# Revit family: Bathtub-American_Standard-Town_Square_Suite-2748_Series
name_source: partatom
category: Plumbing Fixtures
revit_build: Autodesk Revit 2014 (Build: 20130308_1515(x64)
units: mm (PartAtom-declared; Revit-internal decimal feet)

## types (9) — shared parameters
Apron: 9460.018 (specify color) = No
Assembly Code = D2010510
CW Connection = Yes
CWFU = 3
Default Elevation = 0"
Description = TOWN SQUARE® 5' x 42" WHIRLPOOL AND BATHING POOL HIGH GLOSS
EverClean = No
HW Connection = Yes
HWFU = 3
Height = 23"
Length = 41 5/8"
Manufacturer = American Standard
Model = 2748.002.011
Outlet Diameter = 1 1/2"
Outlet Location = 14 1/2"
Product Documentation Link = https://www.americanstandard-us.com
Product Page URL = https://www.americanstandard-us.com
Revised Date = 05/07/2020
Safe-T-Heater*: 9075.120 = No
Tile Bead Kit: 751755-200 = No
URL = https://www.americanstandard-us.com
Vent Connection = No
WFU = 4
Warranty Documentation Link = https://www.americanstandard-us.com
Waste Connection = Yes
Width = 59 1/2"

## per-type parameters (varying)
| type | Finish | Material | multi-directional and flow adjustable jets |
| 2748.002.011 | Americast-American Standard-011-Arctic | Americast-American Standard-011-Arctic | No |
| 2748.002.020 | Americast-American Standard-020-White | Americast-American Standard-020-White | No |
| 2748.002.222 | Americast-American Standard-222-Linen | Americast-American Standard-222-Linen | No |
| 2748.018WC.011 | Americast-American Standard-011-Arctic | Americast-American Standard-011-Arctic | Yes |
| 2748.018WC.020 | Americast-American Standard-020-White | Americast-American Standard-020-White | Yes |
| 2748.018WC.222 | Americast-American Standard-222-Linen | Americast-American Standard-222-Linen | Yes |
| 2748.018WC.K2.011 | Americast-American Standard-011-Arctic | Americast-American Standard-011-Arctic | Yes |
| 2748.018WC.K2.020 | Americast-American Standard-020-White | Americast-American Standard-020-White | Yes |
| 2748.018WC.K2.222 | Americast-American Standard-222-Linen | Americast-American Standard-222-Linen | Yes |

## geometry (parser evidence)
native form markers: Sweep x1
no freeform markers — native parametric forms only
